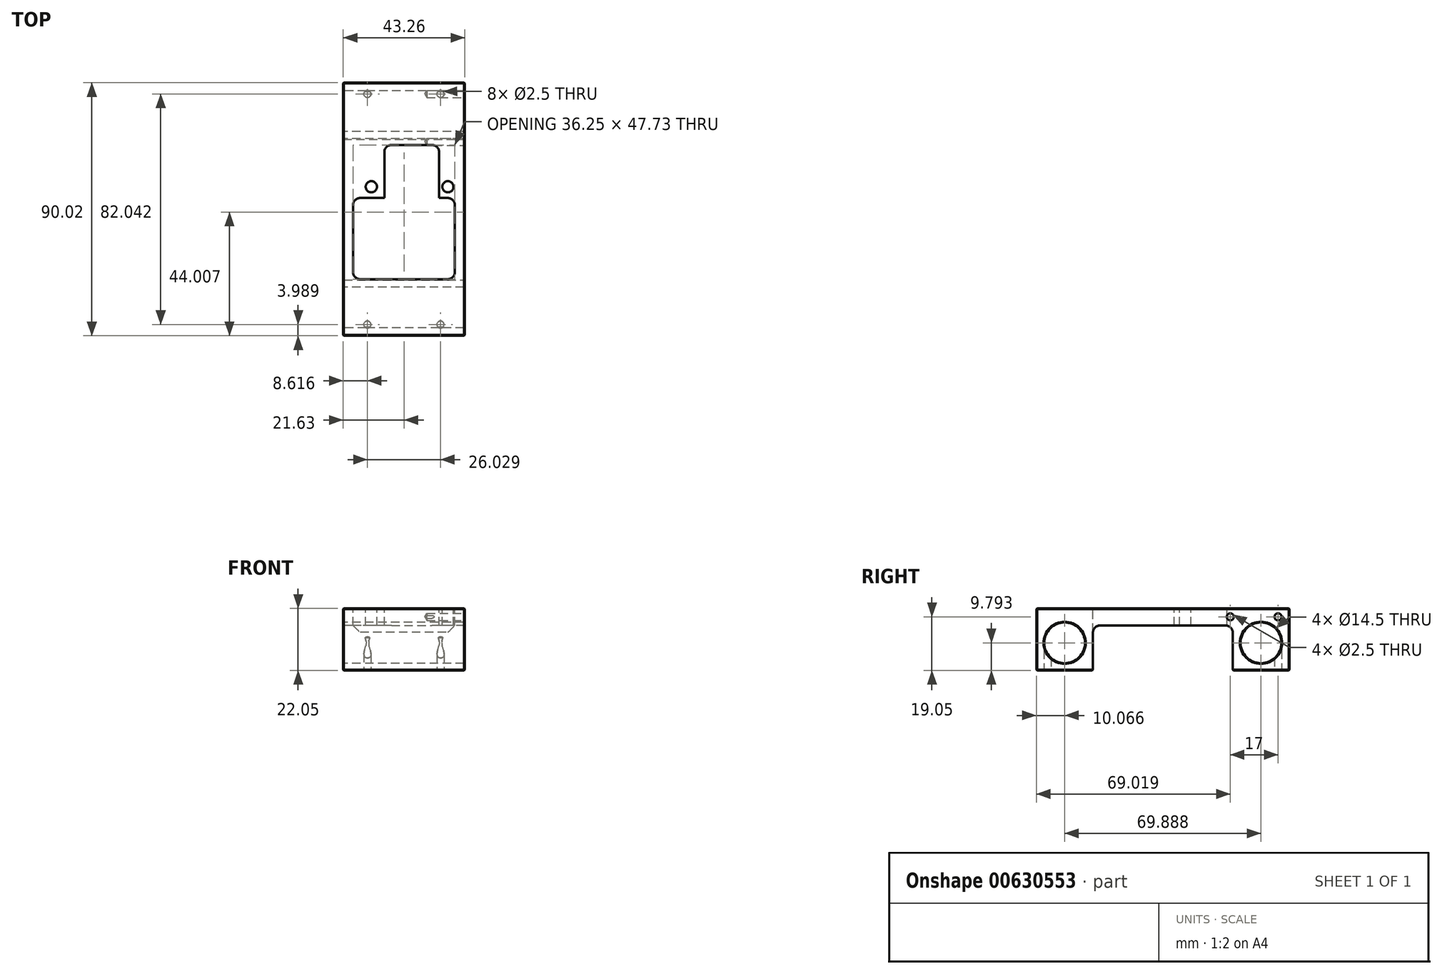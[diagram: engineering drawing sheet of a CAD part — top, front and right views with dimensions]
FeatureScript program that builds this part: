
annotation { "Feature Type Name" : "Feature", "Feature Type Description" : "" }
export const myFeature = defineFeature(function(context is Context, id is Id, definition is map)
    precondition{}
    {
        {
            var Q0;
            Q0=qCreatedBy(makeId("Right.planeOp"),FACE);
            var sketch = newSketch(context, id + "F0", { "sketchPlane" : qUnion([Q0])});
            skLineSegment(sketch, "E0", {"start": v(-45, 0) * mm, "end": v(45, 0) * mm});
            skLineSegment(sketch, "E1.MirrorCS", {"start": v(24.88, -22.05) * mm, "end": v(45, -22.05) * mm});
            skCircle(sketch, "E2.MirrorC", {"center": v(-34.94, -12.26) * mm, "radius": 7.25 * mm});
            skLineSegment(sketch, "E3.MirrorCS", {"start": v(24.88, -6.1) * mm, "end": v(24.88, -22.05) * mm});
            skLineSegment(sketch, "E4.MirrorCS", {"start": v(-24.88, -6.1) * mm, "end": v(24.88, -6.1) * mm});
            skCircle(sketch, "E5.MirrorC", {"center": v(34.94, -12.26) * mm, "radius": 7.25 * mm});
            skLineSegment(sketch, "E6.MirrorCS", {"start": v(45, 0) * mm, "end": v(45, -22.05) * mm});
            skLineSegment(sketch, "E7.MirrorCS", {"start": v(-24.88, -22.05) * mm, "end": v(-24.88, -6.1) * mm});
            skLineSegment(sketch, "E8.MirrorCS", {"start": v(-45, 0) * mm, "end": v(-45, -22.05) * mm});
            skLineSegment(sketch, "E9.MirrorCS", {"start": v(-45, -22.05) * mm, "end": v(-24.88, -22.05) * mm});
            skSolve(sketch);
        }
        {
            var Q0;
            Q0=makeQuery(id+"F0.imprint","IMPRINT",FACE,{"disambiguationData":[TD([[makeQuery(id+"F0.imprint","IMPRINT",EDGE,{"derivedFrom":sQuery(id+"F0.wireOp",EDGE,"E0")}),-1.0]])]});
            extrude(context, id + "F1", {"entities" : qUnion([Q0]), "endBound" : BoundingType.SYMMETRIC, "depth" : 43.25 * mm, "offsetDistance" : 25.4 * mm});
        }
        {
            var Q0;
            Q0=makeQuery(id+"F1.opExtrude","SWEPT_EDGE",EDGE,{"disambiguationData":[OSD([sQuery(id+"F0.wireOp",EDGE,"E4.MirrorCS"),sQuery(id+"F0.wireOp",EDGE,"E7.MirrorCS")])]});
            var Q1;
            Q1=makeQuery(id+"F1.opExtrude","SWEPT_EDGE",EDGE,{"disambiguationData":[OSD([sQuery(id+"F0.wireOp",EDGE,"E4.MirrorCS"),sQuery(id+"F0.wireOp",EDGE,"E3.MirrorCS")])]});
            fillet(context, id + "F2", {"entities" : qUnion([Q0, Q1]), "radius" : 2.54 * mm, "tangentPropagation" : true, "allowEdgeOverflow" : false});
        }
        {
            var Q0;
            Q0=makeQuery(id+"F1.opExtrude","CAP_EDGE",EDGE,{"disambiguationData":[OSD([sQuery(id+"F0.wireOp",EDGE,"E8.MirrorCS")])],"isStart":false});
            var Q1;
            Q1=makeQuery(id+"F1.opExtrude","CAP_EDGE",EDGE,{"disambiguationData":[OSD([sQuery(id+"F0.wireOp",EDGE,"E0")])],"isStart":false});
            var Q2;
            Q2=makeQuery(id+"F1.opExtrude","SWEPT_EDGE",EDGE,{"disambiguationData":[OSD([sQuery(id+"F0.wireOp",EDGE,"E0"),sQuery(id+"F0.wireOp",EDGE,"E8.MirrorCS")])]});
            var Q3;
            Q3=makeQuery(id+"F1.opExtrude","SWEPT_EDGE",EDGE,{"disambiguationData":[OSD([sQuery(id+"F0.wireOp",EDGE,"E8.MirrorCS"),sQuery(id+"F0.wireOp",EDGE,"E9.MirrorCS")])]});
            var Q4;
            Q4=makeQuery(id+"F1.opExtrude","CAP_EDGE",EDGE,{"disambiguationData":[OSD([sQuery(id+"F0.wireOp",EDGE,"E8.MirrorCS")])],"isStart":true});
            var Q5;
            Q5=makeQuery(id+"F1.opExtrude","CAP_EDGE",EDGE,{"disambiguationData":[OSD([sQuery(id+"F0.wireOp",EDGE,"E0")])],"isStart":true});
            var Q6;
            Q6=makeQuery(id+"F1.opExtrude","SWEPT_EDGE",EDGE,{"disambiguationData":[OSD([sQuery(id+"F0.wireOp",EDGE,"E0"),sQuery(id+"F0.wireOp",EDGE,"E6.MirrorCS")])]});
            var Q7;
            Q7=makeQuery(id+"F1.opExtrude","CAP_EDGE",EDGE,{"disambiguationData":[OSD([sQuery(id+"F0.wireOp",EDGE,"E6.MirrorCS")])],"isStart":true});
            var Q8;
            Q8=makeQuery(id+"F1.opExtrude","SWEPT_EDGE",EDGE,{"disambiguationData":[OSD([sQuery(id+"F0.wireOp",EDGE,"E1.MirrorCS"),sQuery(id+"F0.wireOp",EDGE,"E6.MirrorCS")])]});
            var Q9;
            Q9=makeQuery(id+"F1.opExtrude","CAP_EDGE",EDGE,{"disambiguationData":[OSD([sQuery(id+"F0.wireOp",EDGE,"E6.MirrorCS")])],"isStart":false});
            var Q10;
            Q10=makeQuery(id+"F1.opExtrude","CAP_EDGE",EDGE,{"disambiguationData":[OSD([sQuery(id+"F0.wireOp",EDGE,"E5.MirrorC")])],"isStart":false});
            var Q11;
            Q11=makeQuery(id+"F1.opExtrude","CAP_EDGE",EDGE,{"disambiguationData":[OSD([sQuery(id+"F0.wireOp",EDGE,"E2.MirrorC")])],"isStart":false});
            var Q12;
            Q12=makeQuery(id+"F1.opExtrude","CAP_EDGE",EDGE,{"disambiguationData":[OSD([sQuery(id+"F0.wireOp",EDGE,"E2.MirrorC")])],"isStart":true});
            var Q13;
            Q13=makeQuery(id+"F1.opExtrude","CAP_EDGE",EDGE,{"disambiguationData":[OSD([sQuery(id+"F0.wireOp",EDGE,"E5.MirrorC")])],"isStart":true});
            var Q14;
            Q14=makeQuery(id+"F1.opExtrude","CAP_EDGE",EDGE,{"disambiguationData":[OSD([sQuery(id+"F0.wireOp",EDGE,"E1.MirrorCS")])],"isStart":true});
            var Q15;
            Q15=makeQuery(id+"F1.opExtrude","SWEPT_EDGE",EDGE,{"disambiguationData":[OSD([sQuery(id+"F0.wireOp",EDGE,"E1.MirrorCS"),sQuery(id+"F0.wireOp",EDGE,"E3.MirrorCS")])]});
            var Q16;
            Q16=makeQuery(id+"F1.opExtrude","CAP_EDGE",EDGE,{"disambiguationData":[OSD([sQuery(id+"F0.wireOp",EDGE,"E9.MirrorCS")])],"isStart":false});
            var Q17;
            Q17=makeQuery(id+"F1.opExtrude","SWEPT_EDGE",EDGE,{"disambiguationData":[OSD([sQuery(id+"F0.wireOp",EDGE,"E9.MirrorCS"),sQuery(id+"F0.wireOp",EDGE,"E7.MirrorCS")])]});
            var Q18;
            Q18=makeQuery(id+"F1.opExtrude","CAP_EDGE",EDGE,{"disambiguationData":[OSD([sQuery(id+"F0.wireOp",EDGE,"E9.MirrorCS")])],"isStart":true});
            var Q19;
            Q19=makeQuery(id+"F1.opExtrude","CAP_EDGE",EDGE,{"disambiguationData":[OSD([sQuery(id+"F0.wireOp",EDGE,"E1.MirrorCS")])],"isStart":false});
            chamfer(context, id + "F3", {"entities" : qUnion([Q0, Q1, Q2, Q3, Q4, Q5, Q6, Q7, Q8, Q9, Q10, Q11, Q12, Q13, Q14, Q15, Q16, Q17, Q18, Q19]), "width" : 0.25 * mm, "tangentPropagation" : true});
        }
        {
            var Q0;
            Q0=makeQuery(id+"F1.opExtrude","SWEPT_BODY",BODY,{"disambiguationData":[OSD([sQuery(id+"F0.wireOp",EDGE,"E0"),sQuery(id+"F0.wireOp",EDGE,"E8.MirrorCS"),sQuery(id+"F0.wireOp",EDGE,"E2.MirrorC"),sQuery(id+"F0.wireOp",EDGE,"E1.MirrorCS"),sQuery(id+"F0.wireOp",EDGE,"E5.MirrorC"),sQuery(id+"F0.wireOp",EDGE,"E4.MirrorCS"),sQuery(id+"F0.wireOp",EDGE,"E3.MirrorCS"),sQuery(id+"F0.wireOp",EDGE,"E9.MirrorCS"),sQuery(id+"F0.wireOp",EDGE,"E7.MirrorCS"),sQuery(id+"F0.wireOp",EDGE,"E6.MirrorCS")])]});
            transform(context, id + "F4", {"entities" : qUnion([Q0]), "transformType" : TransformType.TRANSLATION_3D, "dx" : 0 * mm, "dy" : 0 * mm, "dz" : 0 * mm, "makeCopy" : true});
        }
        {
            var Q0;
            Q0=makeQuery(id+"F1.opExtrude","SWEPT_FACE",FACE,{"disambiguationData":[OSD([sQuery(id+"F0.wireOp",EDGE,"E9.MirrorCS")])]});
            var sketch = newSketch(context, id + "F5", { "sketchPlane" : qUnion([Q0])});
            skPoint(sketch, "E10", {"position": v(-13.01, 41.02) * mm});
            skPoint(sketch, "E11", {"position": v(13.01, 41.02) * mm});
            skPoint(sketch, "E12", {"position": v(-13.01, -41.02) * mm});
            skPoint(sketch, "E13", {"position": v(13.01, -41.02) * mm});
            skSolve(sketch);
        }
        {
            var Q0;
            Q0=sQuery(id+"F5.wireOp",VERTEX,"E10");
            var Q1;
            Q1=sQuery(id+"F5.wireOp",VERTEX,"E11");
            var Q2;
            Q2=sQuery(id+"F5.wireOp",VERTEX,"E13");
            var Q3;
            Q3=sQuery(id+"F5.wireOp",VERTEX,"E12");
            var Q4;
            Q4=makeQuery(id+"F1.opExtrude","SWEPT_BODY",BODY,{"disambiguationData":[OSD([sQuery(id+"F0.wireOp",EDGE,"E0"),sQuery(id+"F0.wireOp",EDGE,"E8.MirrorCS"),sQuery(id+"F0.wireOp",EDGE,"E2.MirrorC"),sQuery(id+"F0.wireOp",EDGE,"E1.MirrorCS"),sQuery(id+"F0.wireOp",EDGE,"E5.MirrorC"),sQuery(id+"F0.wireOp",EDGE,"E4.MirrorCS"),sQuery(id+"F0.wireOp",EDGE,"E3.MirrorCS"),sQuery(id+"F0.wireOp",EDGE,"E9.MirrorCS"),sQuery(id+"F0.wireOp",EDGE,"E7.MirrorCS"),sQuery(id+"F0.wireOp",EDGE,"E6.MirrorCS")])]});
            hole(context, id + "F6", {"style" : HoleStyle.SIMPLE, "endStyle" : HoleEndStyle.BLIND, "standardTappedOrClearance" : lookupTablePath({ "standard" : "ISO", "engagement" : "75%", "pitch" : "0.5 mm", "size" : "M3", "type" : "Tapped" }), "standardBlindInLast" : lookupTablePath({ "standard" : "ISO", "engagement" : "75%", "pitch" : "0.5 mm", "size" : "M3", "type" : "Tapped" }), "holeDiameter" : 2.5 * mm, "majorDiameter" : 3 * mm, "showTappedDepth" : true, "holeDepth" : 11.66 * mm, "isTappedThrough" : true, "tappedDepth" : 10.16 * mm, "tapClearance" : 3, "locations" : qUnion([Q0, Q1, Q2, Q3]), "scope" : qUnion([Q4])});
        }
        {
            var Q0;
            Q0=makeQuery(id+"F4.opPattern","COPY",BODY,{"derivedFrom":makeQuery(id+"F1.opExtrude","SWEPT_BODY",BODY,{"disambiguationData":[OSD([sQuery(id+"F0.wireOp",EDGE,"E0"),sQuery(id+"F0.wireOp",EDGE,"E8.MirrorCS"),sQuery(id+"F0.wireOp",EDGE,"E2.MirrorC"),sQuery(id+"F0.wireOp",EDGE,"E1.MirrorCS"),sQuery(id+"F0.wireOp",EDGE,"E5.MirrorC"),sQuery(id+"F0.wireOp",EDGE,"E4.MirrorCS"),sQuery(id+"F0.wireOp",EDGE,"E3.MirrorCS"),sQuery(id+"F0.wireOp",EDGE,"E9.MirrorCS"),sQuery(id+"F0.wireOp",EDGE,"E7.MirrorCS"),sQuery(id+"F0.wireOp",EDGE,"E6.MirrorCS")])]}),"instanceName":"1"});
            deleteBodies(context, id + "F7", {"entities" : qUnion([Q0])});
        }
        {
            var Q0;
            Q0=makeQuery(id+"F1.opExtrude","CAP_FACE",FACE,{"disambiguationData":[OSD([sQuery(id+"F0.wireOp",EDGE,"E0"),sQuery(id+"F0.wireOp",EDGE,"E8.MirrorCS"),sQuery(id+"F0.wireOp",EDGE,"E2.MirrorC"),sQuery(id+"F0.wireOp",EDGE,"E1.MirrorCS"),sQuery(id+"F0.wireOp",EDGE,"E5.MirrorC"),sQuery(id+"F0.wireOp",EDGE,"E4.MirrorCS"),sQuery(id+"F0.wireOp",EDGE,"E3.MirrorCS"),sQuery(id+"F0.wireOp",EDGE,"E9.MirrorCS"),sQuery(id+"F0.wireOp",EDGE,"E7.MirrorCS"),sQuery(id+"F0.wireOp",EDGE,"E6.MirrorCS")])],"isStart":false});
            var sketch = newSketch(context, id + "F8", { "sketchPlane" : qUnion([Q0])});
            skPoint(sketch, "E14", {"position": v(24, -3) * mm});
            skPoint(sketch, "E15", {"position": v(41, -3) * mm});
            skSolve(sketch);
        }
        {
            var Q0;
            Q0=sQuery(id+"F8.wireOp",VERTEX,"E14");
            var Q1;
            Q1=sQuery(id+"F8.wireOp",VERTEX,"E15");
            var Q2;
            Q2=makeQuery(id+"F1.opExtrude","SWEPT_BODY",BODY,{"disambiguationData":[OSD([sQuery(id+"F0.wireOp",EDGE,"E0"),sQuery(id+"F0.wireOp",EDGE,"E8.MirrorCS"),sQuery(id+"F0.wireOp",EDGE,"E2.MirrorC"),sQuery(id+"F0.wireOp",EDGE,"E1.MirrorCS"),sQuery(id+"F0.wireOp",EDGE,"E5.MirrorC"),sQuery(id+"F0.wireOp",EDGE,"E4.MirrorCS"),sQuery(id+"F0.wireOp",EDGE,"E3.MirrorCS"),sQuery(id+"F0.wireOp",EDGE,"E9.MirrorCS"),sQuery(id+"F0.wireOp",EDGE,"E7.MirrorCS"),sQuery(id+"F0.wireOp",EDGE,"E6.MirrorCS")])]});
            hole(context, id + "F9", {"style" : HoleStyle.SIMPLE, "endStyle" : HoleEndStyle.BLIND, "standardTappedOrClearance" : lookupTablePath({ "standard" : "ISO", "engagement" : "75%", "pitch" : "0.5 mm", "size" : "M3", "type" : "Tapped" }), "standardBlindInLast" : lookupTablePath({ "standard" : "ISO", "engagement" : "75%", "pitch" : "0.5 mm", "size" : "M3", "type" : "Tapped" }), "holeDiameter" : 2.5 * mm, "majorDiameter" : 3 * mm, "showTappedDepth" : true, "holeDepth" : 13.5 * mm, "isTappedThrough" : true, "tappedDepth" : 12 * mm, "tapClearance" : 3, "locations" : qUnion([Q0, Q1]), "scope" : qUnion([Q2])});
        }
        {
            var Q0;
            Q0=makeQuery(id+"F1.opExtrude","SWEPT_BODY",BODY,{"disambiguationData":[OSD([sQuery(id+"F0.wireOp",EDGE,"E0"),sQuery(id+"F0.wireOp",EDGE,"E8.MirrorCS"),sQuery(id+"F0.wireOp",EDGE,"E2.MirrorC"),sQuery(id+"F0.wireOp",EDGE,"E1.MirrorCS"),sQuery(id+"F0.wireOp",EDGE,"E5.MirrorC"),sQuery(id+"F0.wireOp",EDGE,"E4.MirrorCS"),sQuery(id+"F0.wireOp",EDGE,"E3.MirrorCS"),sQuery(id+"F0.wireOp",EDGE,"E9.MirrorCS"),sQuery(id+"F0.wireOp",EDGE,"E7.MirrorCS"),sQuery(id+"F0.wireOp",EDGE,"E6.MirrorCS")])]});
            transform(context, id + "F10", {"entities" : qUnion([Q0]), "transformType" : TransformType.TRANSLATION_3D, "dx" : 0 * mm, "dy" : 0 * mm, "dz" : 0 * mm, "makeCopy" : true});
        }
        {
            var Q0;
            Q0=makeQuery(id+"F10.opPattern","COPY",FACE,{"derivedFrom":makeQuery(id+"F1.opExtrude","SWEPT_FACE",FACE,{"disambiguationData":[OSD([sQuery(id+"F0.wireOp",EDGE,"E0")])]}),"instanceName":"1"});
            var sketch = newSketch(context, id + "F11", { "sketchPlane" : qUnion([Q0])});
            skLineSegment(sketch, "E16", {"start": v(-15.59, -24.87) * mm, "end": v(15.59, -24.87) * mm});
            skLineSegment(sketch, "E17", {"start": v(18.13, -22.33) * mm, "end": v(18.13, 1.47) * mm});
            skLineSegment(sketch, "E18", {"start": v(15.59, 4.01) * mm, "end": v(12.53, 4.01) * mm});
            skLineSegment(sketch, "E19", {"start": v(12.53, 4.01) * mm, "end": v(12.53, 20.32) * mm});
            skLineSegment(sketch, "E20", {"start": v(10, 22.86) * mm, "end": v(-4.45, 22.86) * mm});
            skLineSegment(sketch, "E21", {"start": v(-7, 20.32) * mm, "end": v(-7, 4.01) * mm});
            skLineSegment(sketch, "E22", {"start": v(-7, 4.01) * mm, "end": v(-15.59, 4.01) * mm});
            skLineSegment(sketch, "E23", {"start": v(-18.13, 1.47) * mm, "end": v(-18.13, -22.33) * mm});
            skPoint(sketch, "E24.visualSharp", {"position": v(-18.13, -24.87) * mm});
            skArc(sketch, "E24.filletArc", {"start": v(-18.13, -22.33) * mm, "mid": v(-17.38, -24.12) * mm, "end": v(-15.59, -24.87) * mm});
            skPoint(sketch, "E25.visualSharp", {"position": v(18.13, -24.87) * mm});
            skArc(sketch, "E25.filletArc", {"start": v(15.59, -24.87) * mm, "mid": v(17.38, -24.12) * mm, "end": v(18.13, -22.33) * mm});
            skPoint(sketch, "E26.visualSharp", {"position": v(18.13, 4.01) * mm});
            skArc(sketch, "E26.filletArc", {"start": v(18.13, 1.47) * mm, "mid": v(17.38, 3.27) * mm, "end": v(15.59, 4.01) * mm});
            skPoint(sketch, "E27.visualSharp", {"position": v(-18.13, 4.01) * mm});
            skArc(sketch, "E27.filletArc", {"start": v(-15.59, 4.01) * mm, "mid": v(-17.38, 3.27) * mm, "end": v(-18.13, 1.47) * mm});
            skPoint(sketch, "E28.visualSharp", {"position": v(-7, 22.86) * mm});
            skArc(sketch, "E28.filletArc", {"start": v(-4.45, 22.86) * mm, "mid": v(-6.25, 22.12) * mm, "end": v(-7, 20.32) * mm});
            skPoint(sketch, "E29.visualSharp", {"position": v(12.53, 22.86) * mm});
            skArc(sketch, "E29.filletArc", {"start": v(12.53, 20.32) * mm, "mid": v(11.79, 22.12) * mm, "end": v(10, 22.86) * mm});
            skPoint(sketch, "E30", {"position": v(-11.62, 8) * mm});
            skPoint(sketch, "E31", {"position": v(15.62, 8) * mm});
            skSolve(sketch);
        }
        {
            var Q0;
            Q0=sQuery(id+"F11.wireOp",VERTEX,"E30");
            var Q1;
            Q1=sQuery(id+"F11.wireOp",VERTEX,"E31");
            var Q2;
            Q2=makeQuery(id+"F10.opPattern","COPY",BODY,{"derivedFrom":makeQuery(id+"F1.opExtrude","SWEPT_BODY",BODY,{"disambiguationData":[OSD([sQuery(id+"F0.wireOp",EDGE,"E0"),sQuery(id+"F0.wireOp",EDGE,"E8.MirrorCS"),sQuery(id+"F0.wireOp",EDGE,"E2.MirrorC"),sQuery(id+"F0.wireOp",EDGE,"E1.MirrorCS"),sQuery(id+"F0.wireOp",EDGE,"E5.MirrorC"),sQuery(id+"F0.wireOp",EDGE,"E4.MirrorCS"),sQuery(id+"F0.wireOp",EDGE,"E3.MirrorCS"),sQuery(id+"F0.wireOp",EDGE,"E9.MirrorCS"),sQuery(id+"F0.wireOp",EDGE,"E7.MirrorCS"),sQuery(id+"F0.wireOp",EDGE,"E6.MirrorCS")])]}),"instanceName":"1"});
            hole(context, id + "F12", {"style" : HoleStyle.SIMPLE, "endStyle" : HoleEndStyle.THROUGH, "standardTappedOrClearance" : lookupTablePath({ "standard" : "ISO", "size" : "4", "type" : "Drilled" }), "standardBlindInLast" : lookupTablePath({ "standard" : "ISO", "size" : "4", "type" : "Drilled" }), "holeDiameter" : 4 * mm, "majorDiameter" : 3 * mm, "isTappedThrough" : true, "tappedDepth" : 12 * mm, "tapClearance" : 3, "locations" : qUnion([Q0, Q1]), "scope" : qUnion([Q2])});
        }
        {
            var Q0;
            Q0=makeQuery(id+"F11.imprint","IMPRINT",FACE,{"disambiguationData":[TD([[makeQuery(id+"F11.imprint","IMPRINT",EDGE,{"derivedFrom":sQuery(id+"F11.wireOp",EDGE,"E16")}),1.0]])]});
            extrude(context, id + "F13", {"entities" : qUnion([Q0]), "operationType" : NewBodyOperationType.REMOVE, "oppositeDirection" : true, "depth" : 25.4 * mm, "offsetDistance" : 25.4 * mm});
        }
    });
